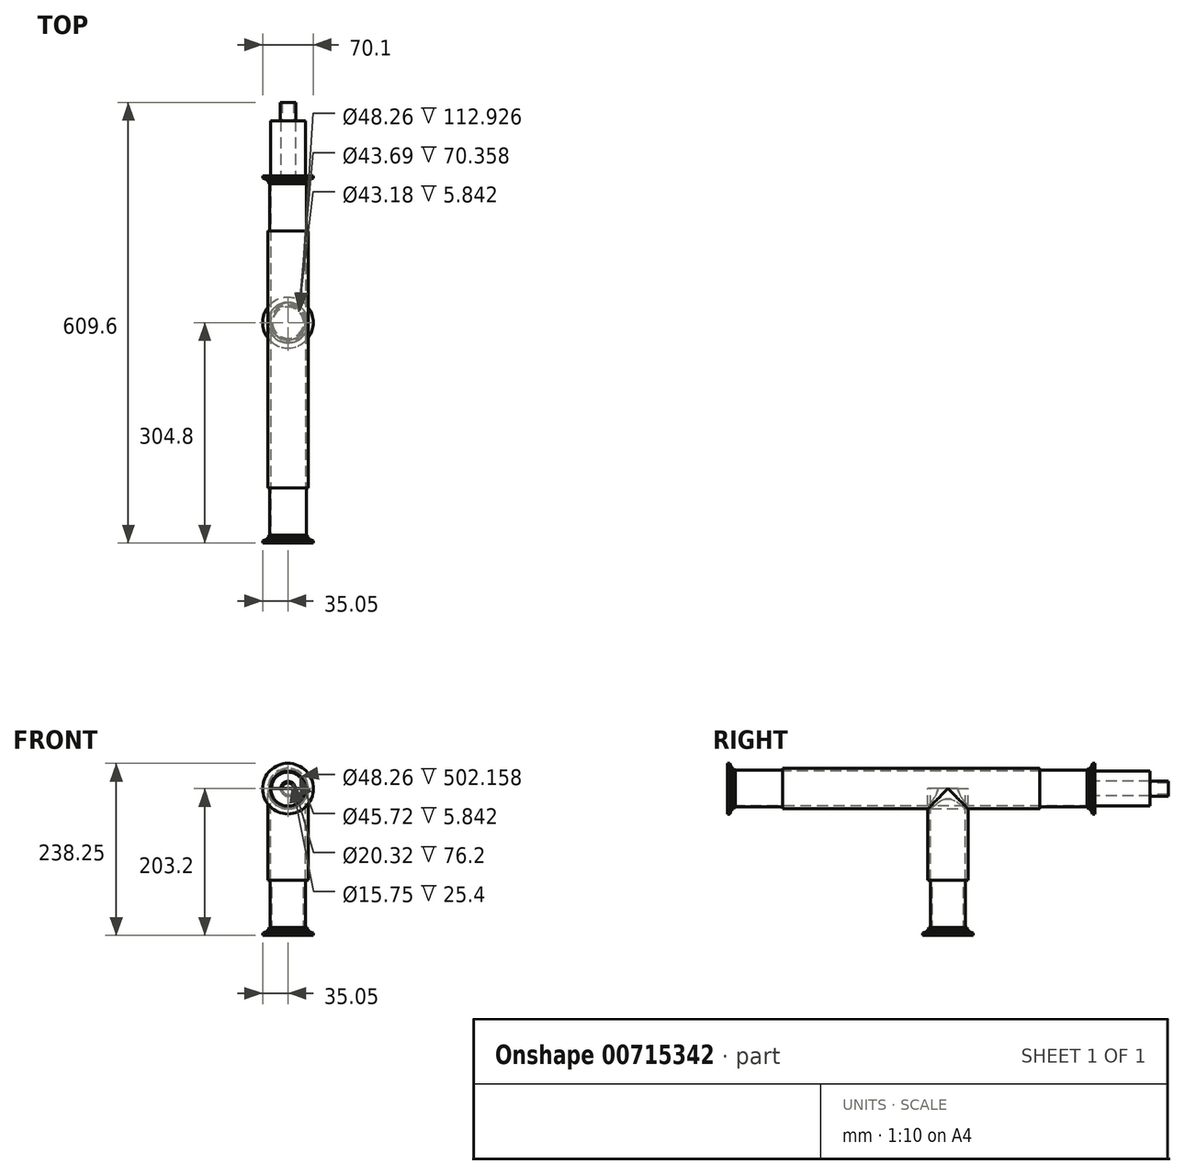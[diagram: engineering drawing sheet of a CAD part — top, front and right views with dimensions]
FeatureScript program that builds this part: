
annotation { "Feature Type Name" : "Feature", "Feature Type Description" : "" }
export const myFeature = defineFeature(function(context is Context, id is Id, definition is map)
    precondition{}
    {
        {
            var Q0;
            Q0=qCreatedBy(makeId("Front.planeOp"),FACE);
            var sketch = newSketch(context, id + "F0", { "sketchPlane" : qUnion([Q0])});
            skCircle(sketch, "E0", {"center": v(0, 0) * mm, "radius": 22.23 * mm, "construction": true});
            skSolve(sketch);
        }
        {
            var Q0;
            Q0=qCreatedBy(makeId("Front.planeOp"),FACE);
            var sketch = newSketch(context, id + "F1", { "sketchPlane" : qUnion([Q0])});
            skCircle(sketch, "E1", {"center": v(0, 0) * mm, "radius": 24.13 * mm});
            skCircle(sketch, "E2", {"center": v(0, 0) * mm, "radius": 35.05 * mm});
            skSolve(sketch);
        }
        {
            var Q0;
            Q0=qSketchRegion(id+"F1",true);
            extrude(context, id + "F2", {"entities" : qUnion([Q0]), "oppositeDirection" : true, "depth" : 5.84 * mm, "offsetDistance" : 25.4 * mm});
        }
        {
            var Q0;
            Q0=makeQuery(id+"F2.opExtrude","CAP_EDGE",EDGE,{"disambiguationData":[OSD([sQuery(id+"F1.wireOp",EDGE,"E2")])],"isStart":false});
            chamfer(context, id + "F3", {"entities" : qUnion([Q0]), "chamferType" : ChamferType.OFFSET_ANGLE, "width" : 2.54 * mm, "oppositeDirection" : false, "angle" : 70 * degree, "tangentPropagation" : true});
        }
        {
            var Q0;
            Q0=makeQuery(id+"F2.opExtrude","CAP_FACE",FACE,{"disambiguationData":[OSD([sQuery(id+"F1.wireOp",EDGE,"E1"),sQuery(id+"F1.wireOp",EDGE,"E2")])],"isStart":false});
            var sketch = newSketch(context, id + "F4", { "sketchPlane" : qUnion([Q0])});
            skCircle(sketch, "E3", {"center": v(0, 0) * mm, "radius": 28.07 * mm});
            skCircle(sketch, "E4", {"center": v(0, 0) * mm, "radius": 24.13 * mm});
            skSolve(sketch);
        }
        {
            var Q0;
            Q0=qSketchRegion(id+"F4",true);
            extrude(context, id + "F5", {"entities" : qUnion([Q0]), "operationType" : NewBodyOperationType.ADD, "depth" : 2.54 * mm, "offsetDistance" : 25.4 * mm});
        }
        {
            var Q0;
            Q0=makeQuery(id+"F5.opExtrude","CAP_FACE",FACE,{"disambiguationData":[OSD([sQuery(id+"F4.wireOp",EDGE,"E3"),sQuery(id+"F4.wireOp",EDGE,"E4")])],"isStart":false});
            var sketch = newSketch(context, id + "F6", { "sketchPlane" : qUnion([Q0])});
            skCircle(sketch, "E5", {"center": v(0, 0) * mm, "radius": 26.55 * mm});
            skCircle(sketch, "E6", {"center": v(0, 0) * mm, "radius": 24.13 * mm});
            skSolve(sketch);
        }
        {
            var Q0;
            Q0=qSketchRegion(id+"F6",true);
            extrude(context, id + "F7", {"entities" : qUnion([Q0]), "operationType" : NewBodyOperationType.ADD, "depth" : 2.54 * mm, "offsetDistance" : 25.4 * mm});
        }
        {
            var Q0;
            Q0=makeQuery(id+"F7.opExtrude","CAP_FACE",FACE,{"disambiguationData":[OSD([sQuery(id+"F6.wireOp",EDGE,"E5"),sQuery(id+"F6.wireOp",EDGE,"E6")])],"isStart":false});
            var sketch = newSketch(context, id + "F8", { "sketchPlane" : qUnion([Q0])});
            skCircle(sketch, "E7", {"center": v(0, 0) * mm, "radius": 24.13 * mm});
            skCircle(sketch, "E8", {"center": v(0, 0) * mm, "radius": 25.4 * mm});
            skSolve(sketch);
        }
        {
            var Q0;
            Q0=qSketchRegion(id+"F8",true);
            extrude(context, id + "F9", {"entities" : qUnion([Q0]), "operationType" : NewBodyOperationType.ADD, "depth" : 65.28 * mm, "offsetDistance" : 25.4 * mm});
        }
        {
            var Q0;
            Q0=makeQuery(id+"F9.opExtrude","CAP_FACE",FACE,{"disambiguationData":[OSD([sQuery(id+"F8.wireOp",EDGE,"E7"),sQuery(id+"F8.wireOp",EDGE,"E8")])],"isStart":false});
            var sketch = newSketch(context, id + "F10", { "sketchPlane" : qUnion([Q0])});
            skCircle(sketch, "E9", {"center": v(0, 0) * mm, "radius": 27.94 * mm});
            skCircle(sketch, "E10", {"center": v(0, 0) * mm, "radius": 24.13 * mm});
            skSolve(sketch);
        }
        {
            var Q0;
            Q0=qCreatedBy(makeId("Right.planeOp"),FACE);
            var sketch = newSketch(context, id + "F11", { "sketchPlane" : qUnion([Q0])});
            skLineSegment(sketch, "E11", {"start": v(76.2, 0) * mm, "end": v(431.8, 0) * mm});
            skSolve(sketch);
        }
        {
            var Q0;
            Q0=qSketchRegion(id+"F10",true);
            var Q1;
            Q1=qConstructionFilter(qBodyType(qCreatedBy(id+"F11",EDGE),BodyType.WIRE),ConstructionObject.NO);
            sweep(context, id + "F12", {"operationType" : NewBodyOperationType.ADD, "profiles" : qUnion([Q0]), "path" : qUnion([Q1])});
        }
        {
            var Q0;
            Q0=makeQuery(id+"F12.opSweep","CAP_FACE",FACE,{"disambiguationData":[OSD([sQuery(id+"F10.wireOp",EDGE,"E9"),sQuery(id+"F10.wireOp",EDGE,"E10"),sQuery(id+"F11.wireOp",VERTEX,"7ykRA0Qg-2DrY-rTCa-7tXY-ZQoEE0Xzwcjr.end")])],"isStart":false});
            var sketch = newSketch(context, id + "F13", { "sketchPlane" : qUnion([Q0])});
            skCircle(sketch, "E12", {"center": v(0, 0) * mm, "radius": 24.13 * mm});
            skCircle(sketch, "E13", {"center": v(0, 0) * mm, "radius": 25.4 * mm});
            skSolve(sketch);
        }
        {
            var Q0;
            Q0=makeQuery(id+"F12.opSweep","CAP_EDGE",EDGE,{"disambiguationData":[OSD([sQuery(id+"F10.wireOp",EDGE,"E9"),sQuery(id+"F11.wireOp",VERTEX,"7ykRA0Qg-2DrY-rTCa-7tXY-ZQoEE0Xzwcjr.end")])],"isStart":false});
            fillet(context, id + "F14", {"entities" : qUnion([Q0]), "radius" : 1.27 * mm, "tangentPropagation" : true, "allowEdgeOverflow" : false});
        }
        {
            var Q0;
            Q0=qSketchRegion(id+"F13",true);
            extrude(context, id + "F15", {"entities" : qUnion([Q0]), "operationType" : NewBodyOperationType.ADD, "depth" : 76.2 * mm, "offsetDistance" : 25.4 * mm});
        }
        {
            var Q0;
            Q0=makeQuery(id+"F15.opExtrude","CAP_FACE",FACE,{"disambiguationData":[OSD([sQuery(id+"F13.wireOp",EDGE,"E12"),sQuery(id+"F13.wireOp",EDGE,"E13")])],"isStart":false});
            var sketch = newSketch(context, id + "F16", { "sketchPlane" : qUnion([Q0])});
            skCircle(sketch, "E14", {"center": v(0, 0) * mm, "radius": 35.05 * mm});
            skCircle(sketch, "E15", {"center": v(0, 0) * mm, "radius": 22.86 * mm});
            skSolve(sketch);
        }
        {
            var Q0;
            Q0=qSketchRegion(id+"F16",true);
            extrude(context, id + "F17", {"entities" : qUnion([Q0]), "operationType" : NewBodyOperationType.ADD, "oppositeDirection" : true, "depth" : 5.84 * mm, "offsetDistance" : 25.4 * mm});
        }
        {
            var Q0;
            Q0=makeQuery(id+"F17.opExtrude","CAP_EDGE",EDGE,{"disambiguationData":[OSD([sQuery(id+"F16.wireOp",EDGE,"E14")])],"isStart":false});
            chamfer(context, id + "F18", {"entities" : qUnion([Q0]), "chamferType" : ChamferType.OFFSET_ANGLE, "width" : 2.54 * mm, "oppositeDirection" : false, "angle" : 70 * degree, "tangentPropagation" : true});
        }
        {
            var Q0;
            Q0=makeQuery(id+"F17.opExtrude","CAP_FACE",FACE,{"disambiguationData":[OSD([sQuery(id+"F16.wireOp",EDGE,"E14"),sQuery(id+"F16.wireOp",EDGE,"E15")])],"isStart":false});
            var sketch = newSketch(context, id + "F19", { "sketchPlane" : qUnion([Q0])});
            skCircle(sketch, "E16", {"center": v(0, 0) * mm, "radius": 24.13 * mm});
            skCircle(sketch, "E17", {"center": v(0, 0) * mm, "radius": 28.07 * mm});
            skSolve(sketch);
        }
        {
            var Q0;
            Q0=qSketchRegion(id+"F19",true);
            extrude(context, id + "F20", {"entities" : qUnion([Q0]), "operationType" : NewBodyOperationType.ADD, "depth" : 2.54 * mm, "offsetDistance" : 25.4 * mm});
        }
        {
            var Q0;
            Q0=makeQuery(id+"F20.opExtrude","CAP_FACE",FACE,{"disambiguationData":[OSD([sQuery(id+"F19.wireOp",EDGE,"E16"),sQuery(id+"F19.wireOp",EDGE,"E17")])],"isStart":false});
            var sketch = newSketch(context, id + "F21", { "sketchPlane" : qUnion([Q0])});
            skCircle(sketch, "E18", {"center": v(0, 0) * mm, "radius": 24.13 * mm});
            skCircle(sketch, "E19", {"center": v(0, 0) * mm, "radius": 26.8 * mm});
            skSolve(sketch);
        }
        {
            var Q0;
            Q0=qSketchRegion(id+"F21",true);
            extrude(context, id + "F22", {"entities" : qUnion([Q0]), "operationType" : NewBodyOperationType.ADD, "depth" : 2.54 * mm, "offsetDistance" : 25.4 * mm});
        }
        {
            var Q0;
            Q0=makeQuery(id+"F17.boolean.opBoolean","MERGE",FACE,{"derivedFrom":[makeQuery(id+"F15.opExtrude","CAP_FACE",FACE,{"disambiguationData":[OSD([sQuery(id+"F13.wireOp",EDGE,"E12"),sQuery(id+"F13.wireOp",EDGE,"E13")])],"isStart":false}),makeQuery(id+"F17.opExtrude","CAP_FACE",FACE,{"disambiguationData":[OSD([sQuery(id+"F16.wireOp",EDGE,"E14"),sQuery(id+"F16.wireOp",EDGE,"E15")])],"isStart":true})]});
            var sketch = newSketch(context, id + "F23", { "sketchPlane" : qUnion([Q0])});
            skCircle(sketch, "E20", {"center": v(0, 0) * mm, "radius": 10.16 * mm});
            skCircle(sketch, "E21", {"center": v(0, 0) * mm, "radius": 24.13 * mm});
            skSolve(sketch);
        }
        {
            var Q0;
            Q0=qSketchRegion(id+"F23",true);
            extrude(context, id + "F24", {"entities" : qUnion([Q0]), "operationType" : NewBodyOperationType.ADD, "depth" : 76.2 * mm, "offsetDistance" : 25.4 * mm});
        }
        {
            var Q0;
            Q0=makeQuery(id+"F24.opExtrude","CAP_FACE",FACE,{"disambiguationData":[OSD([sQuery(id+"F23.wireOp",EDGE,"E20"),sQuery(id+"F23.wireOp",EDGE,"E21")])],"isStart":false});
            var sketch = newSketch(context, id + "F25", { "sketchPlane" : qUnion([Q0])});
            skCircle(sketch, "E22", {"center": v(0, 0) * mm, "radius": 10.67 * mm});
            skCircle(sketch, "E23", {"center": v(0, 0) * mm, "radius": 7.87 * mm});
            skSolve(sketch);
        }
        {
            var Q0;
            Q0=qSketchRegion(id+"F25",true);
            extrude(context, id + "F26", {"entities" : qUnion([Q0]), "operationType" : NewBodyOperationType.ADD, "depth" : 25.4 * mm, "offsetDistance" : 25.4 * mm});
        }
        {
            var Q0;
            Q0=qCreatedBy(makeId("Right.planeOp"),FACE);
            var sketch = newSketch(context, id + "F27", { "sketchPlane" : qUnion([Q0])});
            skLineSegment(sketch, "E24", {"start": v(0, 0) * mm, "end": v(609.6, 0) * mm});
            skSolve(sketch);
        }
        {
            var Q0;
            Q0=qCreatedBy(makeId("Top.planeOp"),FACE);
            var sketch = newSketch(context, id + "F28", { "sketchPlane" : qUnion([Q0])});
            skCircle(sketch, "E25", {"center": v(0, 304.8) * mm, "radius": 27.94 * mm});
            skCircle(sketch, "E26", {"center": v(0, 304.8) * mm, "radius": 24.13 * mm});
            skSolve(sketch);
        }
        {
            var Q0;
            Q0=qSketchRegion(id+"F28",true);
            extrude(context, id + "F29", {"entities" : qUnion([Q0]), "operationType" : NewBodyOperationType.ADD, "oppositeDirection" : true, "depth" : 127 * mm, "offsetDistance" : 25.4 * mm});
        }
        {
            var Q0;
            Q0=makeQuery(id+"F29.opExtrude","CAP_FACE",FACE,{"disambiguationData":[OSD([sQuery(id+"F28.wireOp",EDGE,"E25"),sQuery(id+"F28.wireOp",EDGE,"E26")])],"isStart":false});
            var sketch = newSketch(context, id + "F30", { "sketchPlane" : qUnion([Q0])});
            skCircle(sketch, "E27", {"center": v(0, -304.8) * mm, "radius": 24.38 * mm});
            skCircle(sketch, "E28", {"center": v(0, -304.8) * mm, "radius": 21.84 * mm});
            skSolve(sketch);
        }
        {
            var Q0;
            Q0=qSketchRegion(id+"F30",true);
            extrude(context, id + "F31", {"entities" : qUnion([Q0]), "operationType" : NewBodyOperationType.ADD, "depth" : 76.2 * mm, "offsetDistance" : 25.4 * mm});
        }
        {
            var Q0;
            Q0=makeQuery(id+"F31.opExtrude","CAP_FACE",FACE,{"disambiguationData":[OSD([sQuery(id+"F30.wireOp",EDGE,"E27"),sQuery(id+"F30.wireOp",EDGE,"E28")])],"isStart":false});
            var sketch = newSketch(context, id + "F32", { "sketchPlane" : qUnion([Q0])});
            skCircle(sketch, "E29", {"center": v(0, -304.8) * mm, "radius": 21.59 * mm});
            skCircle(sketch, "E30", {"center": v(0, -304.8) * mm, "radius": 35.05 * mm});
            skSolve(sketch);
        }
        {
            var Q0;
            Q0=qSketchRegion(id+"F32",true);
            extrude(context, id + "F33", {"entities" : qUnion([Q0]), "operationType" : NewBodyOperationType.ADD, "oppositeDirection" : true, "depth" : 5.84 * mm, "offsetDistance" : 25.4 * mm});
        }
        {
            var Q0;
            Q0=makeQuery(id+"F33.opExtrude","CAP_EDGE",EDGE,{"disambiguationData":[OSD([sQuery(id+"F32.wireOp",EDGE,"E30")])],"isStart":false});
            chamfer(context, id + "F34", {"entities" : qUnion([Q0]), "chamferType" : ChamferType.OFFSET_ANGLE, "width" : 2.54 * mm, "oppositeDirection" : false, "angle" : 70 * degree, "tangentPropagation" : true});
        }
        {
            var Q0;
            Q0=makeQuery(id+"F33.opExtrude","CAP_FACE",FACE,{"disambiguationData":[OSD([sQuery(id+"F32.wireOp",EDGE,"E29"),sQuery(id+"F32.wireOp",EDGE,"E30")])],"isStart":false});
            var sketch = newSketch(context, id + "F35", { "sketchPlane" : qUnion([Q0])});
            skCircle(sketch, "E31", {"center": v(0, 304.8) * mm, "radius": 28.07 * mm});
            skCircle(sketch, "E32", {"center": v(0, 304.8) * mm, "radius": 24.38 * mm});
            skSolve(sketch);
        }
        {
            var Q0;
            Q0=qSketchRegion(id+"F35",true);
            extrude(context, id + "F36", {"entities" : qUnion([Q0]), "operationType" : NewBodyOperationType.ADD, "depth" : 2.54 * mm, "offsetDistance" : 25.4 * mm});
        }
        {
            var Q0;
            Q0=makeQuery(id+"F36.opExtrude","CAP_FACE",FACE,{"disambiguationData":[OSD([sQuery(id+"F35.wireOp",EDGE,"E31"),sQuery(id+"F35.wireOp",EDGE,"E32")])],"isStart":false});
            var sketch = newSketch(context, id + "F37", { "sketchPlane" : qUnion([Q0])});
            skCircle(sketch, "E33", {"center": v(0, 304.8) * mm, "radius": 26.8 * mm});
            skCircle(sketch, "E34", {"center": v(0, 304.8) * mm, "radius": 24.38 * mm});
            skSolve(sketch);
        }
        {
            var Q0;
            Q0=qSketchRegion(id+"F37",true);
            extrude(context, id + "F38", {"entities" : qUnion([Q0]), "operationType" : NewBodyOperationType.ADD, "depth" : 2.54 * mm, "offsetDistance" : 25.4 * mm});
        }
    });
